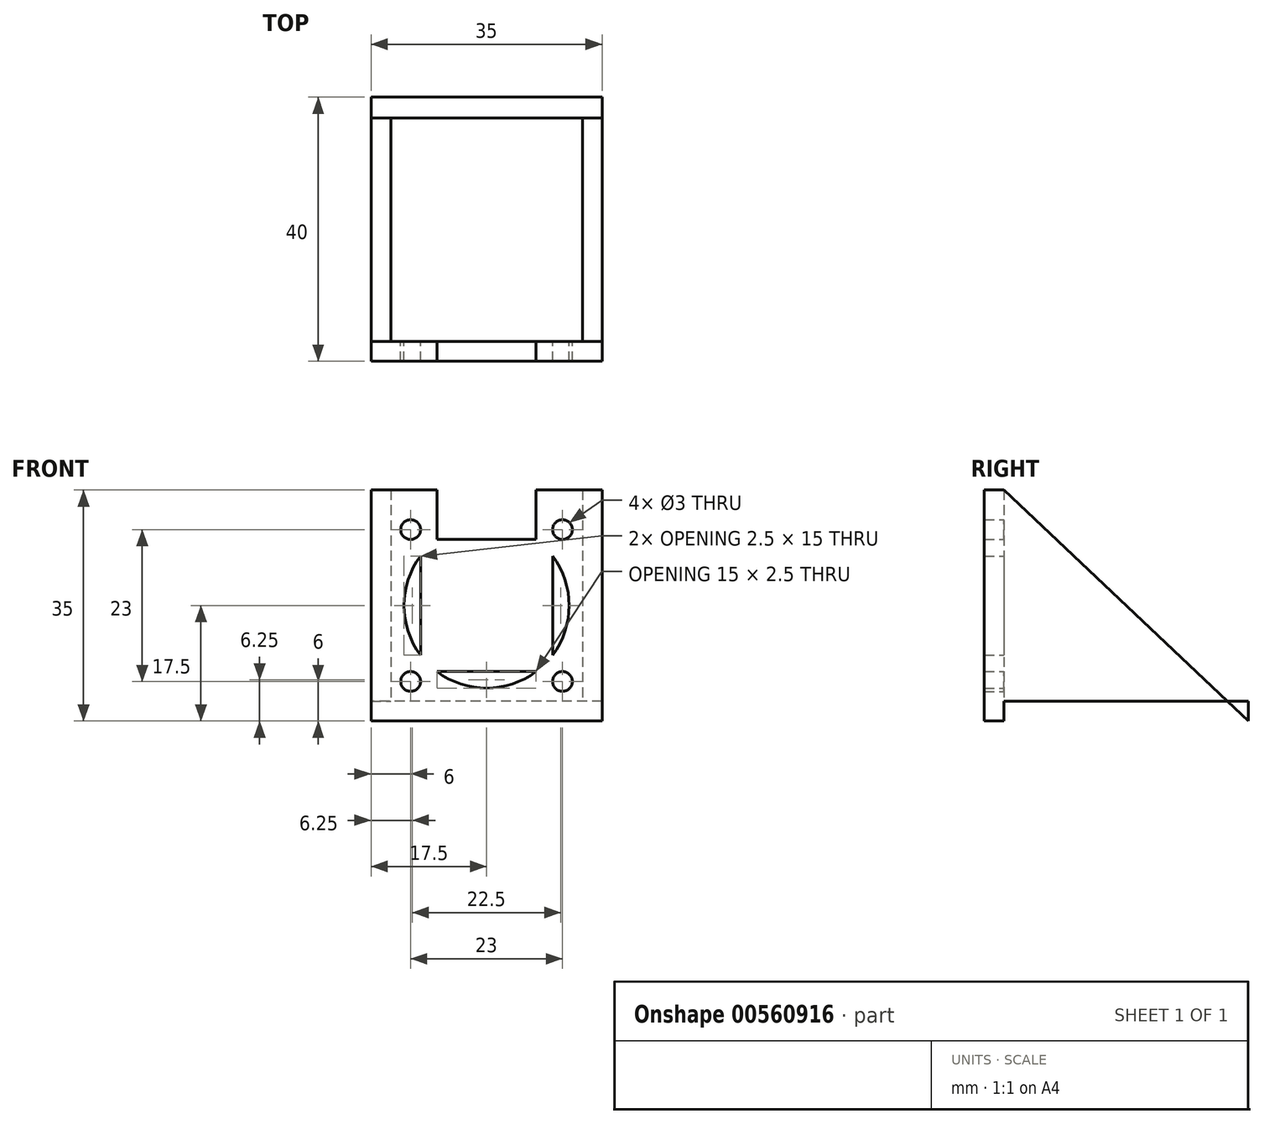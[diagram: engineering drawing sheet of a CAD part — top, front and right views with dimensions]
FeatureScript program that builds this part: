
annotation { "Feature Type Name" : "Feature", "Feature Type Description" : "" }
export const myFeature = defineFeature(function(context is Context, id is Id, definition is map)
    precondition{}
    {
        {
            var Q0;
            Q0=qCreatedBy(makeId("Front.planeOp"),FACE);
            var sketch = newSketch(context, id + "F0", { "sketchPlane" : qUnion([Q0])});
            skLineSegment(sketch, "E0.bottom", {"start": v(-17.5, 17.5) * mm, "end": v(17.5, 17.5) * mm});
            skLineSegment(sketch, "E0.top", {"start": v(-17.5, -17.5) * mm, "end": v(17.5, -17.5) * mm});
            skLineSegment(sketch, "E0.left", {"start": v(-17.5, 17.5) * mm, "end": v(-17.5, -17.5) * mm});
            skLineSegment(sketch, "E0.right", {"start": v(17.5, 17.5) * mm, "end": v(17.5, -17.5) * mm});
            skCircle(sketch, "E1", {"center": v(-11.5, 11.5) * mm, "radius": 1.5 * mm});
            skCircle(sketch, "E2", {"center": v(11.5, 11.5) * mm, "radius": 1.5 * mm});
            skCircle(sketch, "E3", {"center": v(-11.5, -11.5) * mm, "radius": 1.5 * mm});
            skCircle(sketch, "E4", {"center": v(11.5, -11.5) * mm, "radius": 1.5 * mm});
            skLineSegment(sketch, "E5.bottom", {"start": v(-7.5, 17.5) * mm, "end": v(7.5, 17.5) * mm});
            skLineSegment(sketch, "E5.top", {"start": v(-7.5, 10) * mm, "end": v(7.5, 10) * mm});
            skLineSegment(sketch, "E5.left", {"start": v(-7.5, 17.5) * mm, "end": v(-7.5, 10) * mm});
            skLineSegment(sketch, "E5.right", {"start": v(7.5, 17.5) * mm, "end": v(7.5, 10) * mm});
            skCircle(sketch, "E6", {"center": v(0, 0) * mm, "radius": 12.5 * mm});
            skLineSegment(sketch, "E7.bottom", {"start": v(-10, 10) * mm, "end": v(10, 10) * mm});
            skLineSegment(sketch, "E7.top", {"start": v(-10, -10) * mm, "end": v(10, -10) * mm});
            skLineSegment(sketch, "E7.left", {"start": v(-10, 10) * mm, "end": v(-10, -10) * mm});
            skLineSegment(sketch, "E7.right", {"start": v(10, 10) * mm, "end": v(10, -10) * mm});
            skSolve(sketch);
        }
        {
            var Q0;
            Q0=makeQuery(id+"F0.imprint","IMPRINT",FACE,{"disambiguationData":[TD([[makeQuery(id+"F0.imprint","IMPRINT",EDGE,{"derivedFrom":sQuery(id+"F0.wireOp",EDGE,"E0.bottom")}),-1.0]])]});
            var Q1;
            {var subQ0=sQuery(id+"F0.wireOp",EDGE,"E7.bottom");var subQ1=sQuery(id+"F0.wireOp",EDGE,"E6");var subQ2=makeQuery(id+"F0.imprint","INTERSECT",VERTEX,{"disambiguationData":[OD(1.0)],"derivedFrom":[subQ1,subQ0]});Q1=makeQuery(id+"F0.imprint","IMPRINT",FACE,{"disambiguationData":[TD([[makeQuery(id+"F0.imprint","IMPRINT",EDGE,{"disambiguationData":[TD([[subQ2,-1.0]])],"derivedFrom":subQ1}),-1.0]])]});}
            var Q2;
            {var subQ0=sQuery(id+"F0.wireOp",EDGE,"E7.bottom");var subQ1=sQuery(id+"F0.wireOp",EDGE,"E6");var subQ2=makeQuery(id+"F0.imprint","INTERSECT",VERTEX,{"disambiguationData":[OD(0.0)],"derivedFrom":[subQ1,subQ0]});Q2=makeQuery(id+"F0.imprint","IMPRINT",FACE,{"disambiguationData":[TD([[makeQuery(id+"F0.imprint","IMPRINT",EDGE,{"disambiguationData":[TD([[subQ2,1.0]])],"derivedFrom":subQ1}),-1.0]])]});}
            var Q3;
            {var subQ0=sQuery(id+"F0.wireOp",EDGE,"E7.top");var subQ1=sQuery(id+"F0.wireOp",EDGE,"E6");var subQ2=makeQuery(id+"F0.imprint","INTERSECT",VERTEX,{"disambiguationData":[OD(1.0)],"derivedFrom":[subQ1,subQ0]});Q3=makeQuery(id+"F0.imprint","IMPRINT",FACE,{"disambiguationData":[TD([[makeQuery(id+"F0.imprint","IMPRINT",EDGE,{"disambiguationData":[TD([[subQ2,-1.0]])],"derivedFrom":subQ1}),-1.0]])]});}
            var Q4;
            {var subQ0=sQuery(id+"F0.wireOp",EDGE,"E7.left");var subQ1=sQuery(id+"F0.wireOp",EDGE,"E6");var subQ2=makeQuery(id+"F0.imprint","INTERSECT",VERTEX,{"disambiguationData":[OD(1.0)],"derivedFrom":[subQ1,subQ0]});Q4=makeQuery(id+"F0.imprint","IMPRINT",FACE,{"disambiguationData":[TD([[makeQuery(id+"F0.imprint","IMPRINT",EDGE,{"disambiguationData":[TD([[subQ2,-1.0]])],"derivedFrom":subQ1}),-1.0]])]});}
            var Q5;
            {var subQ1=sQuery(id+"F0.wireOp",EDGE,"E6");var subQ5=sQuery(id+"F0.wireOp",EDGE,"E7.left");var subQ6=makeQuery(id+"F0.imprint","INTERSECT",VERTEX,{"disambiguationData":[OD(1.0)],"derivedFrom":[subQ1,subQ5]});Q5=makeQuery(id+"F0.imprint","IMPRINT",FACE,{"disambiguationData":[TD([[makeQuery(id+"F0.imprint","IMPRINT",EDGE,{"disambiguationData":[TD([[subQ6,-1.0]])],"derivedFrom":subQ1}),1.0]])]});}
            extrude(context, id + "F1", {"entities" : qUnion([Q0, Q1, Q2, Q3, Q4, Q5]), "depth" : 3 * mm, "offsetDistance" : 25 * mm});
        }
        {
            var Q0;
            Q0=qCreatedBy(makeId("Right.planeOp"),FACE);
            var sketch = newSketch(context, id + "F2", { "sketchPlane" : qUnion([Q0])});
            skLineSegment(sketch, "E8", {"start": v(0, -17.5) * mm, "end": v(37, -17.5) * mm});
            skLineSegment(sketch, "E9", {"start": v(37, -17.5) * mm, "end": v(0, 17.5) * mm});
            skLineSegment(sketch, "E10", {"start": v(0, 17.5) * mm, "end": v(0, -17.5) * mm});
            skLineSegment(sketch, "E11.bottom", {"start": v(37, -17.5) * mm, "end": v(0, -17.5) * mm});
            skLineSegment(sketch, "E11.top", {"start": v(37, -14.5) * mm, "end": v(0, -14.5) * mm});
            skLineSegment(sketch, "E11.left", {"start": v(37, -17.5) * mm, "end": v(37, -14.5) * mm});
            skLineSegment(sketch, "E11.right", {"start": v(0, -17.5) * mm, "end": v(0, -14.5) * mm});
            skSolve(sketch);
        }
        {
            var Q0;
            {var subQ0=sQuery(id+"F2.wireOp",EDGE,"E11.bottom");Q0=makeQuery(id+"F2.imprint","IMPRINT",FACE,{"disambiguationData":[TD([[makeQuery(id+"F2.imprint","IMPRINT",EDGE,{"derivedFrom":subQ0}),-1.0]])]});}
            var Q1;
            {var subQ0=sQuery(id+"F2.wireOp",EDGE,"E11.left");Q1=makeQuery(id+"F2.imprint","IMPRINT",FACE,{"disambiguationData":[TD([[makeQuery(id+"F2.imprint","IMPRINT",EDGE,{"derivedFrom":subQ0}),1.0]])]});}
            var Q2;
            {var subQ0=sQuery(id+"F2.wireOp",EDGE,"E10");Q2=makeQuery(id+"F2.imprint","IMPRINT",FACE,{"disambiguationData":[TD([[makeQuery(id+"F2.imprint","IMPRINT",EDGE,{"derivedFrom":subQ0}),1.0]])]});}
            extrude(context, id + "F3", {"entities" : qUnion([Q0, Q1, Q2]), "operationType" : NewBodyOperationType.ADD, "depth" : 17.5 * mm, "offsetDistance" : 25 * mm, "hasSecondDirection" : true, "secondDirectionOppositeDirection" : false, "secondDirectionDepth" : 14.5 * mm});
        }
        {
            var Q0;
            {var subQ0=sQuery(id+"F2.wireOp",EDGE,"E11.bottom");Q0=makeQuery(id+"F2.imprint","IMPRINT",FACE,{"disambiguationData":[TD([[makeQuery(id+"F2.imprint","IMPRINT",EDGE,{"derivedFrom":subQ0}),-1.0]])]});}
            var Q1;
            {var subQ0=sQuery(id+"F2.wireOp",EDGE,"E10");Q1=makeQuery(id+"F2.imprint","IMPRINT",FACE,{"disambiguationData":[TD([[makeQuery(id+"F2.imprint","IMPRINT",EDGE,{"derivedFrom":subQ0}),1.0]])]});}
            var Q2;
            {var subQ0=sQuery(id+"F2.wireOp",EDGE,"E11.left");Q2=makeQuery(id+"F2.imprint","IMPRINT",FACE,{"disambiguationData":[TD([[makeQuery(id+"F2.imprint","IMPRINT",EDGE,{"derivedFrom":subQ0}),1.0]])]});}
            extrude(context, id + "F4", {"entities" : qUnion([Q0, Q1, Q2]), "operationType" : NewBodyOperationType.ADD, "oppositeDirection" : true, "depth" : 17.5 * mm, "offsetDistance" : 25 * mm, "hasSecondDirection" : true, "secondDirectionOppositeDirection" : true, "secondDirectionDepth" : 14.5 * mm});
        }
        {
            var Q0;
            {var subQ0=sQuery(id+"F2.wireOp",EDGE,"E11.bottom");Q0=makeQuery(id+"F2.imprint","IMPRINT",FACE,{"disambiguationData":[TD([[makeQuery(id+"F2.imprint","IMPRINT",EDGE,{"derivedFrom":subQ0}),-1.0]])]});}
            var Q1;
            {var subQ0=sQuery(id+"F2.wireOp",EDGE,"E11.left");Q1=makeQuery(id+"F2.imprint","IMPRINT",FACE,{"disambiguationData":[TD([[makeQuery(id+"F2.imprint","IMPRINT",EDGE,{"derivedFrom":subQ0}),1.0]])]});}
            extrude(context, id + "F5", {"entities" : qUnion([Q0, Q1]), "operationType" : NewBodyOperationType.ADD, "depth" : 35 * mm, "offsetDistance" : 25 * mm, "symmetric" : true});
        }
    });
